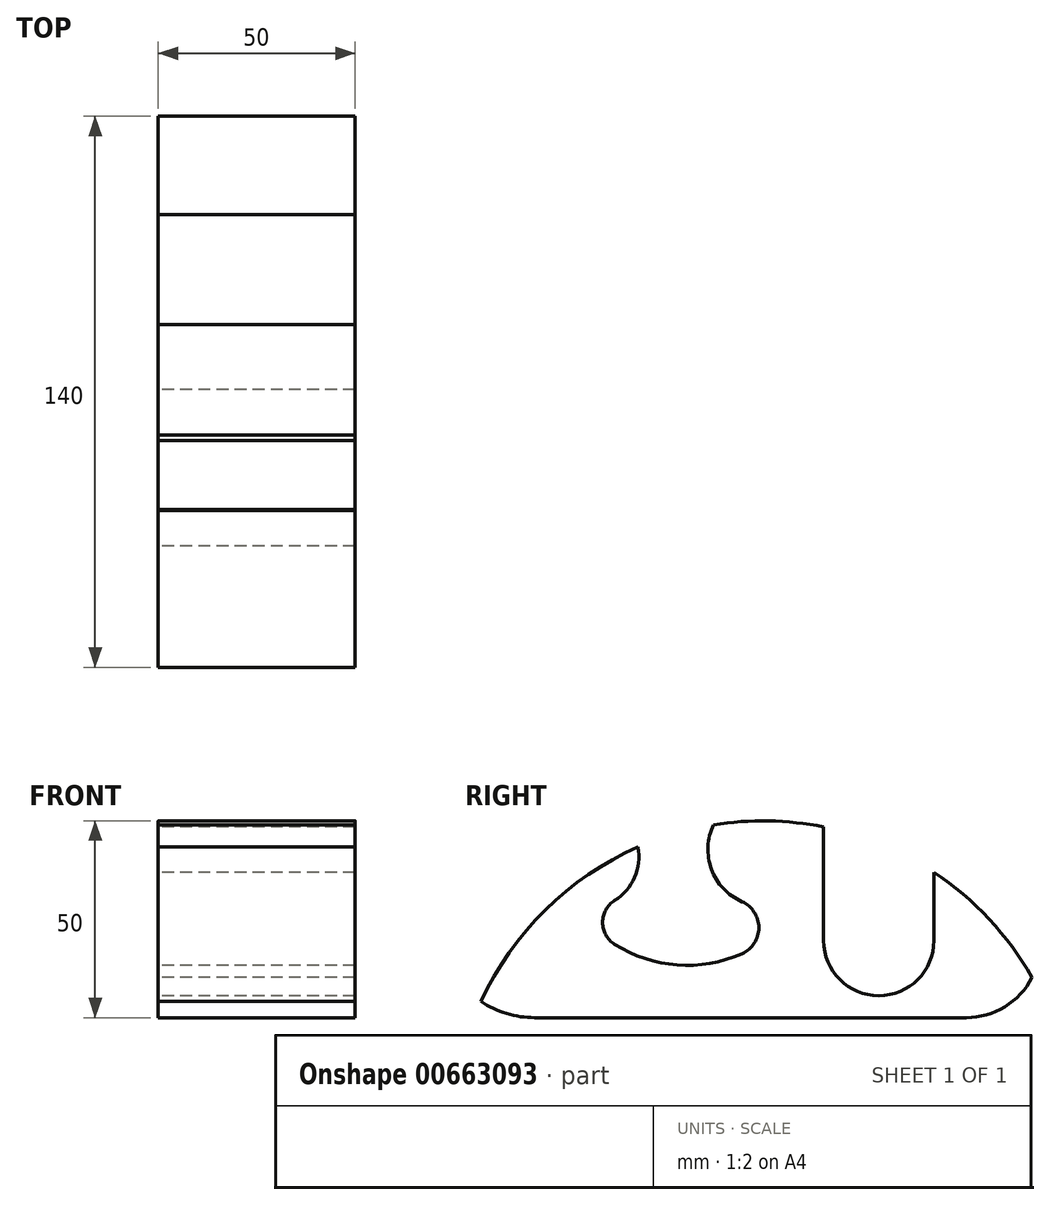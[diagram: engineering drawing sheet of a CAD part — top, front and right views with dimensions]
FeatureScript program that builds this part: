
annotation { "Feature Type Name" : "Feature", "Feature Type Description" : "" }
export const myFeature = defineFeature(function(context is Context, id is Id, definition is map)
    precondition{}
    {
        {
            var Q0;
            Q0=qCreatedBy(makeId("Right.planeOp"),FACE);
            var sketch = newSketch(context, id + "F0", { "sketchPlane" : qUnion([Q0])});
            skArc(sketch, "E0", {"start": v(-64.45, 4.09) * mm, "mid": v(-57.95, 1.04) * mm, "end": v(-50.85, 0) * mm});
            skArc(sketch, "E1", {"start": v(75.55, 10.24) * mm, "mid": v(3.67, 49.92) * mm, "end": v(-64.45, 4.09) * mm});
            skArc(sketch, "E2", {"start": v(58.84, 0) * mm, "mid": v(68.63, 2.76) * mm, "end": v(75.55, 10.24) * mm});
            skLineSegment(sketch, "E3", {"start": v(58.84, 0) * mm, "end": v(-50.85, 0) * mm});
            skLineSegment(sketch, "E4", {"start": v(22.6, 48.47) * mm, "end": v(22.6, 19.58) * mm});
            skArc(sketch, "E5", {"start": v(22.6, 19.58) * mm, "mid": v(36.6, 5.58) * mm, "end": v(50.6, 19.58) * mm});
            skLineSegment(sketch, "E6", {"start": v(50.6, 19.58) * mm, "end": v(50.6, 36.92) * mm});
            skArc(sketch, "E7", {"start": v(-30.51, 18.65) * mm, "mid": v(-14.65, 13.4) * mm, "end": v(1.82, 16.25) * mm});
            skArc(sketch, "E8", {"start": v(-30.51, 29.77) * mm, "mid": v(-33.57, 24.2) * mm, "end": v(-30.51, 18.65) * mm});
            skArc(sketch, "E9", {"start": v(1.82, 16.25) * mm, "mid": v(6.12, 22.86) * mm, "end": v(1.82, 29.47) * mm});
            skArc(sketch, "E10", {"start": v(-5.38, 49) * mm, "mid": v(-5.91, 37.71) * mm, "end": v(1.82, 29.47) * mm});
            skArc(sketch, "E11", {"start": v(-30.51, 29.77) * mm, "mid": v(-25.47, 35.64) * mm, "end": v(-24.59, 43.33) * mm});
            skSolve(sketch);
        }
        {
            var Q0;
            {var subQ3=sQuery(id+"F0.wireOp",EDGE,"E0");Q0=makeQuery(id+"F0.imprint","IMPRINT",FACE,{"disambiguationData":[TD([[makeQuery(id+"F0.imprint","IMPRINT",EDGE,{"derivedFrom":subQ3}),1.0]])]});}
            extrude(context, id + "F1", {"entities" : qUnion([Q0]), "depth" : 50 * mm, "offsetDistance" : 25 * mm});
        }
    });
